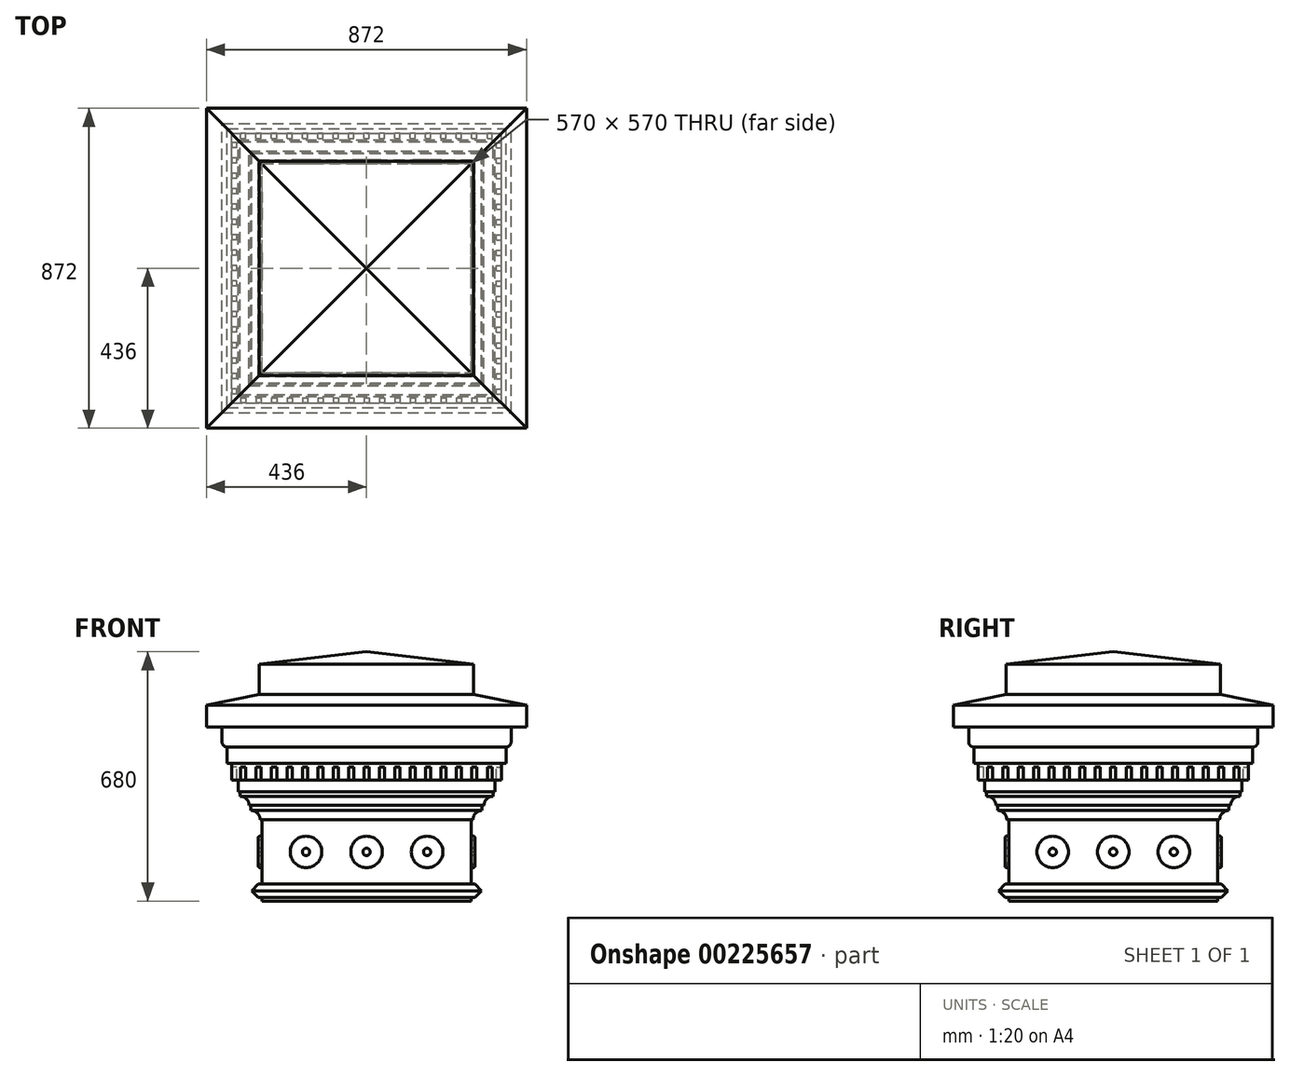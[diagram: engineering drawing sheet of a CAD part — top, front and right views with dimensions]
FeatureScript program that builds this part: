
annotation { "Feature Type Name" : "Feature", "Feature Type Description" : "" }
export const myFeature = defineFeature(function(context is Context, id is Id, definition is map)
    precondition{}
    {
        {
            var Q0;
            Q0=qCreatedBy(makeId("Front.planeOp"),FACE);
            var sketch = newSketch(context, id + "F0", { "sketchPlane" : qUnion([Q0])});
            skLineSegment(sketch, "E0", {"start": v(0, 0) * mm, "end": v(0, 350) * mm});
            skLineSegment(sketch, "E1", {"start": v(0, 350) * mm, "end": v(292, 315.9) * mm});
            skLineSegment(sketch, "E2", {"start": v(292, 315.9) * mm, "end": v(292, 233.9) * mm});
            skLineSegment(sketch, "E3", {"start": v(292, 233.9) * mm, "end": v(436, 204) * mm});
            skLineSegment(sketch, "E4", {"start": v(436, 204) * mm, "end": v(436, 144) * mm});
            skLineSegment(sketch, "E5", {"start": v(436, 144) * mm, "end": v(394, 144) * mm});
            skLineSegment(sketch, "E6", {"start": v(394, 144) * mm, "end": v(394, 104) * mm});
            skArc(sketch, "E7", {"start": v(394, 104) * mm, "mid": v(389.9, 94.1) * mm, "end": v(380, 90) * mm});
            skLineSegment(sketch, "E8", {"start": v(380, 90) * mm, "end": v(380, 46) * mm});
            skLineSegment(sketch, "E9", {"start": v(380, 46) * mm, "end": v(368, 46) * mm});
            skLineSegment(sketch, "E10", {"start": v(368, 46) * mm, "end": v(368, 0) * mm});
            skLineSegment(sketch, "E11", {"start": v(368, 0) * mm, "end": v(0, 0) * mm});
            skLineSegment(sketch, "E12.MirrorCS", {"start": v(-368, 0) * mm, "end": v(0, 0) * mm});
            skLineSegment(sketch, "E13.MirrorCS", {"start": v(0, 350) * mm, "end": v(-292, 315.9) * mm});
            skLineSegment(sketch, "E14.MirrorCS", {"start": v(-436, 144) * mm, "end": v(-394, 144) * mm});
            skLineSegment(sketch, "E15.MirrorCS", {"start": v(-368, 46) * mm, "end": v(-368, 0) * mm});
            skLineSegment(sketch, "E16.MirrorCS", {"start": v(-292, 315.9) * mm, "end": v(-292, 233.9) * mm});
            skLineSegment(sketch, "E17.MirrorCS", {"start": v(-436, 204) * mm, "end": v(-436, 144) * mm});
            skLineSegment(sketch, "E18.MirrorCS", {"start": v(-380, 46) * mm, "end": v(-368, 46) * mm});
            skLineSegment(sketch, "E19.MirrorCS", {"start": v(-292, 233.9) * mm, "end": v(-436, 204) * mm});
            skLineSegment(sketch, "E20.MirrorCS", {"start": v(-380, 90) * mm, "end": v(-380, 46) * mm});
            skArc(sketch, "E21.MirrorCS", {"start": v(-394, 104) * mm, "mid": v(-389.9, 94.1) * mm, "end": v(-380, 90) * mm});
            skLineSegment(sketch, "E22.MirrorCS", {"start": v(-394, 144) * mm, "end": v(-394, 104) * mm});
            skLineSegment(sketch, "E23", {"start": v(0, 350) * mm, "end": v(0, 852.33) * mm});
            skSolve(sketch);
        }
        {
            var Q0;
            Q0=makeQuery(id+"F0.imprint","IMPRINT",FACE,{"disambiguationData":[TD([[makeQuery(id+"F0.imprint","IMPRINT",EDGE,{"derivedFrom":sQuery(id+"F0.wireOp",EDGE,"E0")}),-1.0]])]});
            var Q1;
            Q1=makeQuery(id+"F0.imprint","IMPRINT",FACE,{"disambiguationData":[TD([[makeQuery(id+"F0.imprint","IMPRINT",EDGE,{"derivedFrom":sQuery(id+"F0.wireOp",EDGE,"E0")}),1.0]])]});
            extrude(context, id + "F1", {"entities" : qUnion([Q0, Q1]), "endBound" : BoundingType.SYMMETRIC, "depth" : 900 * mm});
        }
        {
            var Q0;
            Q0=makeQuery(id+"F1.opExtrude","SWEPT_BODY",BODY,{"disambiguationData":[OSD([sQuery(id+"F0.wireOp",EDGE,"E1"),sQuery(id+"F0.wireOp",EDGE,"E2"),sQuery(id+"F0.wireOp",EDGE,"E3"),sQuery(id+"F0.wireOp",EDGE,"E4"),sQuery(id+"F0.wireOp",EDGE,"E5"),sQuery(id+"F0.wireOp",EDGE,"E6"),sQuery(id+"F0.wireOp",EDGE,"E7"),sQuery(id+"F0.wireOp",EDGE,"E8"),sQuery(id+"F0.wireOp",EDGE,"E9"),sQuery(id+"F0.wireOp",EDGE,"E10"),sQuery(id+"F0.wireOp",EDGE,"E11"),sQuery(id+"F0.wireOp",EDGE,"E12.MirrorCS"),sQuery(id+"F0.wireOp",EDGE,"E13.MirrorCS"),sQuery(id+"F0.wireOp",EDGE,"E14.MirrorCS"),sQuery(id+"F0.wireOp",EDGE,"E15.MirrorCS"),sQuery(id+"F0.wireOp",EDGE,"E16.MirrorCS"),sQuery(id+"F0.wireOp",EDGE,"E17.MirrorCS"),sQuery(id+"F0.wireOp",EDGE,"E18.MirrorCS"),sQuery(id+"F0.wireOp",EDGE,"E19.MirrorCS"),sQuery(id+"F0.wireOp",EDGE,"E20.MirrorCS"),sQuery(id+"F0.wireOp",EDGE,"E21.MirrorCS"),sQuery(id+"F0.wireOp",EDGE,"E22.MirrorCS")])]});
            var Q1;
            Q1=sQuery(id+"F0.wireOp",EDGE,"E23");
            var Q2;
            Q2=sQuery(id+"F0.wireOp",EDGE,"E23");
            transform(context, id + "F2", {"entities" : qUnion([Q0]), "transformType" : TransformType.ROTATION, "transformAxis" : qUnion([Q2]), "angle" : 90 * degree, "oppositeDirection" : true, "makeCopy" : true});
        }
        {
            var Q0;
            Q0=makeQuery(id+"F1.opExtrude","SWEPT_BODY",BODY,{"disambiguationData":[OSD([sQuery(id+"F0.wireOp",EDGE,"E1"),sQuery(id+"F0.wireOp",EDGE,"E2"),sQuery(id+"F0.wireOp",EDGE,"E3"),sQuery(id+"F0.wireOp",EDGE,"E4"),sQuery(id+"F0.wireOp",EDGE,"E5"),sQuery(id+"F0.wireOp",EDGE,"E6"),sQuery(id+"F0.wireOp",EDGE,"E7"),sQuery(id+"F0.wireOp",EDGE,"E8"),sQuery(id+"F0.wireOp",EDGE,"E9"),sQuery(id+"F0.wireOp",EDGE,"E10"),sQuery(id+"F0.wireOp",EDGE,"E11"),sQuery(id+"F0.wireOp",EDGE,"E12.MirrorCS"),sQuery(id+"F0.wireOp",EDGE,"E13.MirrorCS"),sQuery(id+"F0.wireOp",EDGE,"E14.MirrorCS"),sQuery(id+"F0.wireOp",EDGE,"E15.MirrorCS"),sQuery(id+"F0.wireOp",EDGE,"E16.MirrorCS"),sQuery(id+"F0.wireOp",EDGE,"E17.MirrorCS"),sQuery(id+"F0.wireOp",EDGE,"E18.MirrorCS"),sQuery(id+"F0.wireOp",EDGE,"E19.MirrorCS"),sQuery(id+"F0.wireOp",EDGE,"E20.MirrorCS"),sQuery(id+"F0.wireOp",EDGE,"E21.MirrorCS"),sQuery(id+"F0.wireOp",EDGE,"E22.MirrorCS")])]});
            var Q1;
            Q1=makeQuery(id+"F2.opPattern","COPY",BODY,{"derivedFrom":makeQuery(id+"F1.opExtrude","SWEPT_BODY",BODY,{"disambiguationData":[OSD([sQuery(id+"F0.wireOp",EDGE,"E1"),sQuery(id+"F0.wireOp",EDGE,"E2"),sQuery(id+"F0.wireOp",EDGE,"E3"),sQuery(id+"F0.wireOp",EDGE,"E4"),sQuery(id+"F0.wireOp",EDGE,"E5"),sQuery(id+"F0.wireOp",EDGE,"E6"),sQuery(id+"F0.wireOp",EDGE,"E7"),sQuery(id+"F0.wireOp",EDGE,"E8"),sQuery(id+"F0.wireOp",EDGE,"E9"),sQuery(id+"F0.wireOp",EDGE,"E10"),sQuery(id+"F0.wireOp",EDGE,"E11"),sQuery(id+"F0.wireOp",EDGE,"E12.MirrorCS"),sQuery(id+"F0.wireOp",EDGE,"E13.MirrorCS"),sQuery(id+"F0.wireOp",EDGE,"E14.MirrorCS"),sQuery(id+"F0.wireOp",EDGE,"E15.MirrorCS"),sQuery(id+"F0.wireOp",EDGE,"E16.MirrorCS"),sQuery(id+"F0.wireOp",EDGE,"E17.MirrorCS"),sQuery(id+"F0.wireOp",EDGE,"E18.MirrorCS"),sQuery(id+"F0.wireOp",EDGE,"E19.MirrorCS"),sQuery(id+"F0.wireOp",EDGE,"E20.MirrorCS"),sQuery(id+"F0.wireOp",EDGE,"E21.MirrorCS"),sQuery(id+"F0.wireOp",EDGE,"E22.MirrorCS")])]}),"instanceName":"1"});
            booleanBodies(context, id + "F3", {"operationType" : BooleanOperationType.INTERSECTION, "tools" : qUnion([Q0, Q1])});
        }
        {
            var Q0;
            Q0=qCreatedBy(makeId("Front.planeOp"),FACE);
            var sketch = newSketch(context, id + "F4", { "sketchPlane" : qUnion([Q0])});
            skLineSegment(sketch, "E24", {"start": v(0, 0) * mm, "end": v(-350, 0) * mm});
            skLineSegment(sketch, "E25", {"start": v(-350, 0) * mm, "end": v(-350, -32) * mm});
            skLineSegment(sketch, "E26", {"start": v(-345, -32) * mm, "end": v(-350, -32) * mm});
            skLineSegment(sketch, "E27", {"start": v(-345, -32) * mm, "end": v(-345, -44) * mm});
            skLineSegment(sketch, "E28", {"start": v(-345, -44) * mm, "end": v(-345, -69) * mm});
            skArc(sketch, "E29", {"start": v(-345, -44) * mm, "mid": v(-327.32, -51.32) * mm, "end": v(-320, -69) * mm});
            skLineSegment(sketch, "E30", {"start": v(-320, -69) * mm, "end": v(-315, -69) * mm});
            skLineSegment(sketch, "E31", {"start": v(-315, -69) * mm, "end": v(-315, -83) * mm});
            skLineSegment(sketch, "E32", {"start": v(-315, -83) * mm, "end": v(-315, -108) * mm});
            skArc(sketch, "E33", {"start": v(-315, -83) * mm, "mid": v(-297.32, -90.32) * mm, "end": v(-290, -108) * mm});
            skLineSegment(sketch, "E34", {"start": v(-290, -108) * mm, "end": v(-285, -108) * mm});
            skLineSegment(sketch, "E35", {"start": v(-285, -108) * mm, "end": v(-285, -284) * mm});
            skLineSegment(sketch, "E36", {"start": v(-285, -284) * mm, "end": v(-295, -284) * mm});
            skLineSegment(sketch, "E37", {"start": v(-295, -284) * mm, "end": v(-313, -302) * mm});
            skLineSegment(sketch, "E38", {"start": v(-313, -302) * mm, "end": v(-295, -320) * mm});
            skLineSegment(sketch, "E39", {"start": v(-295, -320) * mm, "end": v(-285, -320) * mm});
            skLineSegment(sketch, "E40", {"start": v(-285, -320) * mm, "end": v(-285, -330) * mm});
            skLineSegment(sketch, "E41", {"start": v(-285, -330) * mm, "end": v(0, -330) * mm});
            skLineSegment(sketch, "E42", {"start": v(0, 0) * mm, "end": v(0, -330) * mm});
            skLineSegment(sketch, "E43.MirrorCS", {"start": v(0, 0) * mm, "end": v(350, 0) * mm});
            skLineSegment(sketch, "E44.MirrorCS", {"start": v(350, 0) * mm, "end": v(350, -32) * mm});
            skLineSegment(sketch, "E45.MirrorCS", {"start": v(345, -32) * mm, "end": v(350, -32) * mm});
            skLineSegment(sketch, "E46.MirrorCS", {"start": v(345, -32) * mm, "end": v(345, -44) * mm});
            skArc(sketch, "E47.MirrorCS", {"start": v(345, -44) * mm, "mid": v(327.32, -51.32) * mm, "end": v(320, -69) * mm});
            skLineSegment(sketch, "E48.MirrorCS", {"start": v(320, -69) * mm, "end": v(315, -69) * mm});
            skLineSegment(sketch, "E49.MirrorCS", {"start": v(315, -69) * mm, "end": v(315, -83) * mm});
            skArc(sketch, "E50.MirrorCS", {"start": v(315, -83) * mm, "mid": v(297.32, -90.32) * mm, "end": v(290, -108) * mm});
            skLineSegment(sketch, "E51.MirrorCS", {"start": v(290, -108) * mm, "end": v(285, -108) * mm});
            skLineSegment(sketch, "E52.MirrorCS", {"start": v(285, -108) * mm, "end": v(285, -284) * mm});
            skLineSegment(sketch, "E53.MirrorCS", {"start": v(285, -284) * mm, "end": v(295, -284) * mm});
            skLineSegment(sketch, "E54.MirrorCS", {"start": v(295, -284) * mm, "end": v(313, -302) * mm});
            skLineSegment(sketch, "E55.MirrorCS", {"start": v(313, -302) * mm, "end": v(295, -320) * mm});
            skLineSegment(sketch, "E56.MirrorCS", {"start": v(295, -320) * mm, "end": v(285, -320) * mm});
            skLineSegment(sketch, "E57.MirrorCS", {"start": v(285, -320) * mm, "end": v(285, -330) * mm});
            skLineSegment(sketch, "E58.MirrorCS", {"start": v(285, -330) * mm, "end": v(0, -330) * mm});
            skSolve(sketch);
        }
        {
            var Q0;
            Q0=makeQuery(id+"F4.imprint","IMPRINT",FACE,{"disambiguationData":[TD([[makeQuery(id+"F4.imprint","IMPRINT",EDGE,{"derivedFrom":sQuery(id+"F4.wireOp",EDGE,"E42")}),1.0]])]});
            var Q1;
            Q1=makeQuery(id+"F4.imprint","IMPRINT",FACE,{"disambiguationData":[TD([[makeQuery(id+"F4.imprint","IMPRINT",EDGE,{"derivedFrom":sQuery(id+"F4.wireOp",EDGE,"E24")}),1.0]])]});
            extrude(context, id + "F5", {"entities" : qUnion([Q0, Q1]), "endBound" : BoundingType.SYMMETRIC, "depth" : 900 * mm});
        }
        {
            var Q0;
            Q0=makeQuery(id+"F5.opExtrude","SWEPT_BODY",BODY,{"disambiguationData":[OSD([sQuery(id+"F4.wireOp",EDGE,"E24"),sQuery(id+"F4.wireOp",EDGE,"E25"),sQuery(id+"F4.wireOp",EDGE,"E26"),sQuery(id+"F4.wireOp",EDGE,"E27"),sQuery(id+"F4.wireOp",EDGE,"E29"),sQuery(id+"F4.wireOp",EDGE,"E30"),sQuery(id+"F4.wireOp",EDGE,"E31"),sQuery(id+"F4.wireOp",EDGE,"E33"),sQuery(id+"F4.wireOp",EDGE,"E34"),sQuery(id+"F4.wireOp",EDGE,"E35"),sQuery(id+"F4.wireOp",EDGE,"E36"),sQuery(id+"F4.wireOp",EDGE,"E37"),sQuery(id+"F4.wireOp",EDGE,"E38"),sQuery(id+"F4.wireOp",EDGE,"E39"),sQuery(id+"F4.wireOp",EDGE,"E40"),sQuery(id+"F4.wireOp",EDGE,"E41"),sQuery(id+"F4.wireOp",EDGE,"E43.MirrorCS"),sQuery(id+"F4.wireOp",EDGE,"E44.MirrorCS"),sQuery(id+"F4.wireOp",EDGE,"E45.MirrorCS"),sQuery(id+"F4.wireOp",EDGE,"E46.MirrorCS"),sQuery(id+"F4.wireOp",EDGE,"E47.MirrorCS"),sQuery(id+"F4.wireOp",EDGE,"E48.MirrorCS"),sQuery(id+"F4.wireOp",EDGE,"E49.MirrorCS"),sQuery(id+"F4.wireOp",EDGE,"E50.MirrorCS"),sQuery(id+"F4.wireOp",EDGE,"E51.MirrorCS"),sQuery(id+"F4.wireOp",EDGE,"E52.MirrorCS"),sQuery(id+"F4.wireOp",EDGE,"E53.MirrorCS"),sQuery(id+"F4.wireOp",EDGE,"E54.MirrorCS"),sQuery(id+"F4.wireOp",EDGE,"E55.MirrorCS"),sQuery(id+"F4.wireOp",EDGE,"E56.MirrorCS"),sQuery(id+"F4.wireOp",EDGE,"E57.MirrorCS"),sQuery(id+"F4.wireOp",EDGE,"E58.MirrorCS")])]});
            var Q1;
            Q1=sQuery(id+"F4.wireOp",EDGE,"E42");
            transform(context, id + "F6", {"entities" : qUnion([Q0]), "transformType" : TransformType.ROTATION, "transformAxis" : qUnion([Q1]), "angle" : 90 * degree, "makeCopy" : true});
        }
        {
            var Q0;
            Q0=makeQuery(id+"F5.opExtrude","SWEPT_BODY",BODY,{"disambiguationData":[OSD([sQuery(id+"F4.wireOp",EDGE,"E24"),sQuery(id+"F4.wireOp",EDGE,"E25"),sQuery(id+"F4.wireOp",EDGE,"E26"),sQuery(id+"F4.wireOp",EDGE,"E27"),sQuery(id+"F4.wireOp",EDGE,"E29"),sQuery(id+"F4.wireOp",EDGE,"E30"),sQuery(id+"F4.wireOp",EDGE,"E31"),sQuery(id+"F4.wireOp",EDGE,"E33"),sQuery(id+"F4.wireOp",EDGE,"E34"),sQuery(id+"F4.wireOp",EDGE,"E35"),sQuery(id+"F4.wireOp",EDGE,"E36"),sQuery(id+"F4.wireOp",EDGE,"E37"),sQuery(id+"F4.wireOp",EDGE,"E38"),sQuery(id+"F4.wireOp",EDGE,"E39"),sQuery(id+"F4.wireOp",EDGE,"E40"),sQuery(id+"F4.wireOp",EDGE,"E41"),sQuery(id+"F4.wireOp",EDGE,"E43.MirrorCS"),sQuery(id+"F4.wireOp",EDGE,"E44.MirrorCS"),sQuery(id+"F4.wireOp",EDGE,"E45.MirrorCS"),sQuery(id+"F4.wireOp",EDGE,"E46.MirrorCS"),sQuery(id+"F4.wireOp",EDGE,"E47.MirrorCS"),sQuery(id+"F4.wireOp",EDGE,"E48.MirrorCS"),sQuery(id+"F4.wireOp",EDGE,"E49.MirrorCS"),sQuery(id+"F4.wireOp",EDGE,"E50.MirrorCS"),sQuery(id+"F4.wireOp",EDGE,"E51.MirrorCS"),sQuery(id+"F4.wireOp",EDGE,"E52.MirrorCS"),sQuery(id+"F4.wireOp",EDGE,"E53.MirrorCS"),sQuery(id+"F4.wireOp",EDGE,"E54.MirrorCS"),sQuery(id+"F4.wireOp",EDGE,"E55.MirrorCS"),sQuery(id+"F4.wireOp",EDGE,"E56.MirrorCS"),sQuery(id+"F4.wireOp",EDGE,"E57.MirrorCS"),sQuery(id+"F4.wireOp",EDGE,"E58.MirrorCS")])]});
            var Q1;
            Q1=makeQuery(id+"F6.opPattern","COPY",BODY,{"derivedFrom":makeQuery(id+"F5.opExtrude","SWEPT_BODY",BODY,{"disambiguationData":[OSD([sQuery(id+"F4.wireOp",EDGE,"E24"),sQuery(id+"F4.wireOp",EDGE,"E25"),sQuery(id+"F4.wireOp",EDGE,"E26"),sQuery(id+"F4.wireOp",EDGE,"E27"),sQuery(id+"F4.wireOp",EDGE,"E29"),sQuery(id+"F4.wireOp",EDGE,"E30"),sQuery(id+"F4.wireOp",EDGE,"E31"),sQuery(id+"F4.wireOp",EDGE,"E33"),sQuery(id+"F4.wireOp",EDGE,"E34"),sQuery(id+"F4.wireOp",EDGE,"E35"),sQuery(id+"F4.wireOp",EDGE,"E36"),sQuery(id+"F4.wireOp",EDGE,"E37"),sQuery(id+"F4.wireOp",EDGE,"E38"),sQuery(id+"F4.wireOp",EDGE,"E39"),sQuery(id+"F4.wireOp",EDGE,"E40"),sQuery(id+"F4.wireOp",EDGE,"E41"),sQuery(id+"F4.wireOp",EDGE,"E43.MirrorCS"),sQuery(id+"F4.wireOp",EDGE,"E44.MirrorCS"),sQuery(id+"F4.wireOp",EDGE,"E45.MirrorCS"),sQuery(id+"F4.wireOp",EDGE,"E46.MirrorCS"),sQuery(id+"F4.wireOp",EDGE,"E47.MirrorCS"),sQuery(id+"F4.wireOp",EDGE,"E48.MirrorCS"),sQuery(id+"F4.wireOp",EDGE,"E49.MirrorCS"),sQuery(id+"F4.wireOp",EDGE,"E50.MirrorCS"),sQuery(id+"F4.wireOp",EDGE,"E51.MirrorCS"),sQuery(id+"F4.wireOp",EDGE,"E52.MirrorCS"),sQuery(id+"F4.wireOp",EDGE,"E53.MirrorCS"),sQuery(id+"F4.wireOp",EDGE,"E54.MirrorCS"),sQuery(id+"F4.wireOp",EDGE,"E55.MirrorCS"),sQuery(id+"F4.wireOp",EDGE,"E56.MirrorCS"),sQuery(id+"F4.wireOp",EDGE,"E57.MirrorCS"),sQuery(id+"F4.wireOp",EDGE,"E58.MirrorCS")])]}),"instanceName":"1"});
            booleanBodies(context, id + "F7", {"operationType" : BooleanOperationType.INTERSECTION, "tools" : qUnion([Q0, Q1])});
        }
        {
            var Q0;
            Q0=makeQuery(id+"F2.opPattern","COPY",FACE,{"derivedFrom":makeQuery(id+"F1.opExtrude","SWEPT_FACE",FACE,{"disambiguationData":[OSD([sQuery(id+"F0.wireOp",EDGE,"E10")])]}),"instanceName":"1"});
            var sketch = newSketch(context, id + "F8", { "sketchPlane" : qUnion([Q0])});
            skLineSegment(sketch, "E59", {"start": v(0, 0) * mm, "end": v(0, 36) * mm});
            skLineSegment(sketch, "E60", {"start": v(0, 36) * mm, "end": v(-7, 36) * mm});
            skLineSegment(sketch, "E61", {"start": v(-7, 36) * mm, "end": v(-7, 0) * mm});
            skLineSegment(sketch, "E62", {"start": v(-7, 0) * mm, "end": v(0, 0) * mm});
            skLineSegment(sketch, "E63.MirrorCS", {"start": v(0, 36) * mm, "end": v(7, 36) * mm});
            skLineSegment(sketch, "E64.MirrorCS", {"start": v(7, 36) * mm, "end": v(7, 0) * mm});
            skLineSegment(sketch, "E65.MirrorCS", {"start": v(7, 0) * mm, "end": v(0, 0) * mm});
            skLineSegment(sketch, "E66.1.0.0", {"start": v(35, 36) * mm, "end": v(35, 0) * mm});
            skLineSegment(sketch, "E66.1.0.1", {"start": v(35, 0) * mm, "end": v(42, 0) * mm});
            skLineSegment(sketch, "E66.1.0.2", {"start": v(42, 36) * mm, "end": v(35, 36) * mm});
            skLineSegment(sketch, "E66.1.0.3", {"start": v(49, 36) * mm, "end": v(49, 0) * mm});
            skLineSegment(sketch, "E66.1.0.4", {"start": v(49, 0) * mm, "end": v(42, 0) * mm});
            skLineSegment(sketch, "E66.1.0.5", {"start": v(42, 36) * mm, "end": v(49, 36) * mm});
            skLineSegment(sketch, "E66.2.0.0", {"start": v(77, 36) * mm, "end": v(77, 0) * mm});
            skLineSegment(sketch, "E66.2.0.1", {"start": v(77, 0) * mm, "end": v(84, 0) * mm});
            skLineSegment(sketch, "E66.2.0.2", {"start": v(84, 36) * mm, "end": v(77, 36) * mm});
            skLineSegment(sketch, "E66.2.0.3", {"start": v(91, 36) * mm, "end": v(91, 0) * mm});
            skLineSegment(sketch, "E66.2.0.4", {"start": v(91, 0) * mm, "end": v(84, 0) * mm});
            skLineSegment(sketch, "E66.2.0.5", {"start": v(84, 36) * mm, "end": v(91, 36) * mm});
            skLineSegment(sketch, "E66.3.0.0", {"start": v(119, 36) * mm, "end": v(119, 0) * mm});
            skLineSegment(sketch, "E66.3.0.1", {"start": v(119, 0) * mm, "end": v(126, 0) * mm});
            skLineSegment(sketch, "E66.3.0.2", {"start": v(126, 36) * mm, "end": v(119, 36) * mm});
            skLineSegment(sketch, "E66.3.0.3", {"start": v(133, 36) * mm, "end": v(133, 0) * mm});
            skLineSegment(sketch, "E66.3.0.4", {"start": v(133, 0) * mm, "end": v(126, 0) * mm});
            skLineSegment(sketch, "E66.3.0.5", {"start": v(126, 36) * mm, "end": v(133, 36) * mm});
            skLineSegment(sketch, "E66.4.0.0", {"start": v(161, 36) * mm, "end": v(161, 0) * mm});
            skLineSegment(sketch, "E66.4.0.1", {"start": v(161, 0) * mm, "end": v(168, 0) * mm});
            skLineSegment(sketch, "E66.4.0.2", {"start": v(168, 36) * mm, "end": v(161, 36) * mm});
            skLineSegment(sketch, "E66.4.0.3", {"start": v(175, 36) * mm, "end": v(175, 0) * mm});
            skLineSegment(sketch, "E66.4.0.4", {"start": v(175, 0) * mm, "end": v(168, 0) * mm});
            skLineSegment(sketch, "E66.4.0.5", {"start": v(168, 36) * mm, "end": v(175, 36) * mm});
            skLineSegment(sketch, "E66.5.0.0", {"start": v(203, 36) * mm, "end": v(203, 0) * mm});
            skLineSegment(sketch, "E66.5.0.1", {"start": v(203, 0) * mm, "end": v(210, 0) * mm});
            skLineSegment(sketch, "E66.5.0.2", {"start": v(210, 36) * mm, "end": v(203, 36) * mm});
            skLineSegment(sketch, "E66.5.0.3", {"start": v(217, 36) * mm, "end": v(217, 0) * mm});
            skLineSegment(sketch, "E66.5.0.4", {"start": v(217, 0) * mm, "end": v(210, 0) * mm});
            skLineSegment(sketch, "E66.5.0.5", {"start": v(210, 36) * mm, "end": v(217, 36) * mm});
            skLineSegment(sketch, "E66.6.0.0", {"start": v(245, 36) * mm, "end": v(245, 0) * mm});
            skLineSegment(sketch, "E66.6.0.1", {"start": v(245, 0) * mm, "end": v(252, 0) * mm});
            skLineSegment(sketch, "E66.6.0.2", {"start": v(252, 36) * mm, "end": v(245, 36) * mm});
            skLineSegment(sketch, "E66.6.0.3", {"start": v(259, 36) * mm, "end": v(259, 0) * mm});
            skLineSegment(sketch, "E66.6.0.4", {"start": v(259, 0) * mm, "end": v(252, 0) * mm});
            skLineSegment(sketch, "E66.6.0.5", {"start": v(252, 36) * mm, "end": v(259, 36) * mm});
            skLineSegment(sketch, "E66.7.0.0", {"start": v(287, 36) * mm, "end": v(287, 0) * mm});
            skLineSegment(sketch, "E66.7.0.1", {"start": v(287, 0) * mm, "end": v(294, 0) * mm});
            skLineSegment(sketch, "E66.7.0.2", {"start": v(294, 36) * mm, "end": v(287, 36) * mm});
            skLineSegment(sketch, "E66.7.0.3", {"start": v(301, 36) * mm, "end": v(301, 0) * mm});
            skLineSegment(sketch, "E66.7.0.4", {"start": v(301, 0) * mm, "end": v(294, 0) * mm});
            skLineSegment(sketch, "E66.7.0.5", {"start": v(294, 36) * mm, "end": v(301, 36) * mm});
            skLineSegment(sketch, "E66.8.0.0", {"start": v(329, 36) * mm, "end": v(329, 0) * mm});
            skLineSegment(sketch, "E66.8.0.1", {"start": v(329, 0) * mm, "end": v(336, 0) * mm});
            skLineSegment(sketch, "E66.8.0.2", {"start": v(336, 36) * mm, "end": v(329, 36) * mm});
            skLineSegment(sketch, "E66.8.0.3", {"start": v(343, 36) * mm, "end": v(343, 0) * mm});
            skLineSegment(sketch, "E66.8.0.4", {"start": v(343, 0) * mm, "end": v(336, 0) * mm});
            skLineSegment(sketch, "E66.8.0.5", {"start": v(336, 36) * mm, "end": v(343, 36) * mm});
            skLineSegment(sketch, "E66.direction1", {"start": v(-7, 36) * mm, "end": v(35, 36) * mm, "construction": true});
            skLineSegment(sketch, "E67.1.0.0", {"start": v(-49, 36) * mm, "end": v(-49, 0) * mm});
            skLineSegment(sketch, "E67.1.0.1", {"start": v(-49, 0) * mm, "end": v(-42, 0) * mm});
            skLineSegment(sketch, "E67.1.0.2", {"start": v(-42, 36) * mm, "end": v(-49, 36) * mm});
            skLineSegment(sketch, "E67.1.0.3", {"start": v(-35, 36) * mm, "end": v(-35, 0) * mm});
            skLineSegment(sketch, "E67.1.0.4", {"start": v(-35, 0) * mm, "end": v(-42, 0) * mm});
            skLineSegment(sketch, "E67.1.0.5", {"start": v(-42, 36) * mm, "end": v(-35, 36) * mm});
            skLineSegment(sketch, "E67.2.0.0", {"start": v(-91, 36) * mm, "end": v(-91, 0) * mm});
            skLineSegment(sketch, "E67.2.0.1", {"start": v(-91, 0) * mm, "end": v(-84, 0) * mm});
            skLineSegment(sketch, "E67.2.0.2", {"start": v(-84, 36) * mm, "end": v(-91, 36) * mm});
            skLineSegment(sketch, "E67.2.0.3", {"start": v(-77, 36) * mm, "end": v(-77, 0) * mm});
            skLineSegment(sketch, "E67.2.0.4", {"start": v(-77, 0) * mm, "end": v(-84, 0) * mm});
            skLineSegment(sketch, "E67.2.0.5", {"start": v(-84, 36) * mm, "end": v(-77, 36) * mm});
            skLineSegment(sketch, "E67.3.0.0", {"start": v(-133, 36) * mm, "end": v(-133, 0) * mm});
            skLineSegment(sketch, "E67.3.0.1", {"start": v(-133, 0) * mm, "end": v(-126, 0) * mm});
            skLineSegment(sketch, "E67.3.0.2", {"start": v(-126, 36) * mm, "end": v(-133, 36) * mm});
            skLineSegment(sketch, "E67.3.0.3", {"start": v(-119, 36) * mm, "end": v(-119, 0) * mm});
            skLineSegment(sketch, "E67.3.0.4", {"start": v(-119, 0) * mm, "end": v(-126, 0) * mm});
            skLineSegment(sketch, "E67.3.0.5", {"start": v(-126, 36) * mm, "end": v(-119, 36) * mm});
            skLineSegment(sketch, "E67.4.0.0", {"start": v(-175, 36) * mm, "end": v(-175, 0) * mm});
            skLineSegment(sketch, "E67.4.0.1", {"start": v(-175, 0) * mm, "end": v(-168, 0) * mm});
            skLineSegment(sketch, "E67.4.0.2", {"start": v(-168, 36) * mm, "end": v(-175, 36) * mm});
            skLineSegment(sketch, "E67.4.0.3", {"start": v(-161, 36) * mm, "end": v(-161, 0) * mm});
            skLineSegment(sketch, "E67.4.0.4", {"start": v(-161, 0) * mm, "end": v(-168, 0) * mm});
            skLineSegment(sketch, "E67.4.0.5", {"start": v(-168, 36) * mm, "end": v(-161, 36) * mm});
            skLineSegment(sketch, "E67.5.0.0", {"start": v(-217, 36) * mm, "end": v(-217, 0) * mm});
            skLineSegment(sketch, "E67.5.0.1", {"start": v(-217, 0) * mm, "end": v(-210, 0) * mm});
            skLineSegment(sketch, "E67.5.0.2", {"start": v(-210, 36) * mm, "end": v(-217, 36) * mm});
            skLineSegment(sketch, "E67.5.0.3", {"start": v(-203, 36) * mm, "end": v(-203, 0) * mm});
            skLineSegment(sketch, "E67.5.0.4", {"start": v(-203, 0) * mm, "end": v(-210, 0) * mm});
            skLineSegment(sketch, "E67.5.0.5", {"start": v(-210, 36) * mm, "end": v(-203, 36) * mm});
            skLineSegment(sketch, "E67.6.0.0", {"start": v(-259, 36) * mm, "end": v(-259, 0) * mm});
            skLineSegment(sketch, "E67.6.0.1", {"start": v(-259, 0) * mm, "end": v(-252, 0) * mm});
            skLineSegment(sketch, "E67.6.0.2", {"start": v(-252, 36) * mm, "end": v(-259, 36) * mm});
            skLineSegment(sketch, "E67.6.0.3", {"start": v(-245, 36) * mm, "end": v(-245, 0) * mm});
            skLineSegment(sketch, "E67.6.0.4", {"start": v(-245, 0) * mm, "end": v(-252, 0) * mm});
            skLineSegment(sketch, "E67.6.0.5", {"start": v(-252, 36) * mm, "end": v(-245, 36) * mm});
            skLineSegment(sketch, "E67.7.0.0", {"start": v(-301, 36) * mm, "end": v(-301, 0) * mm});
            skLineSegment(sketch, "E67.7.0.1", {"start": v(-301, 0) * mm, "end": v(-294, 0) * mm});
            skLineSegment(sketch, "E67.7.0.2", {"start": v(-294, 36) * mm, "end": v(-301, 36) * mm});
            skLineSegment(sketch, "E67.7.0.3", {"start": v(-287, 36) * mm, "end": v(-287, 0) * mm});
            skLineSegment(sketch, "E67.7.0.4", {"start": v(-287, 0) * mm, "end": v(-294, 0) * mm});
            skLineSegment(sketch, "E67.7.0.5", {"start": v(-294, 36) * mm, "end": v(-287, 36) * mm});
            skLineSegment(sketch, "E67.8.0.0", {"start": v(-343, 36) * mm, "end": v(-343, 0) * mm});
            skLineSegment(sketch, "E67.8.0.1", {"start": v(-343, 0) * mm, "end": v(-336, 0) * mm});
            skLineSegment(sketch, "E67.8.0.2", {"start": v(-336, 36) * mm, "end": v(-343, 36) * mm});
            skLineSegment(sketch, "E67.8.0.3", {"start": v(-329, 36) * mm, "end": v(-329, 0) * mm});
            skLineSegment(sketch, "E67.8.0.4", {"start": v(-329, 0) * mm, "end": v(-336, 0) * mm});
            skLineSegment(sketch, "E67.8.0.5", {"start": v(-336, 36) * mm, "end": v(-329, 36) * mm});
            skLineSegment(sketch, "E67.direction1", {"start": v(-7, 36) * mm, "end": v(-49, 36) * mm, "construction": true});
            skSolve(sketch);
        }
        {
            var Q0;
            Q0=makeQuery(id+"F1.opExtrude","SWEPT_FACE",FACE,{"disambiguationData":[OSD([sQuery(id+"F0.wireOp",EDGE,"E10")])]});
            var sketch = newSketch(context, id + "F9", { "sketchPlane" : qUnion([Q0])});
            skLineSegment(sketch, "E68", {"start": v(0, 0) * mm, "end": v(-7, 0) * mm});
            skLineSegment(sketch, "E69", {"start": v(-7, 0) * mm, "end": v(-7, 36) * mm});
            skLineSegment(sketch, "E70", {"start": v(-7, 36) * mm, "end": v(7, 36) * mm});
            skLineSegment(sketch, "E71", {"start": v(7, 36) * mm, "end": v(7, 0) * mm});
            skLineSegment(sketch, "E72", {"start": v(7, 0) * mm, "end": v(0, 0) * mm});
            skLineSegment(sketch, "E73.1.0.0", {"start": v(35, 0) * mm, "end": v(35, 36) * mm});
            skLineSegment(sketch, "E73.1.0.1", {"start": v(49, 36) * mm, "end": v(49, 0) * mm});
            skLineSegment(sketch, "E73.1.0.2", {"start": v(49, 0) * mm, "end": v(42, 0) * mm});
            skLineSegment(sketch, "E73.1.0.3", {"start": v(35, 36) * mm, "end": v(49, 36) * mm});
            skLineSegment(sketch, "E73.1.0.4", {"start": v(42, 0) * mm, "end": v(35, 0) * mm});
            skLineSegment(sketch, "E73.2.0.0", {"start": v(77, 0) * mm, "end": v(77, 36) * mm});
            skLineSegment(sketch, "E73.2.0.1", {"start": v(91, 36) * mm, "end": v(91, 0) * mm});
            skLineSegment(sketch, "E73.2.0.2", {"start": v(91, 0) * mm, "end": v(84, 0) * mm});
            skLineSegment(sketch, "E73.2.0.3", {"start": v(77, 36) * mm, "end": v(91, 36) * mm});
            skLineSegment(sketch, "E73.2.0.4", {"start": v(84, 0) * mm, "end": v(77, 0) * mm});
            skLineSegment(sketch, "E73.3.0.0", {"start": v(119, 0) * mm, "end": v(119, 36) * mm});
            skLineSegment(sketch, "E73.3.0.1", {"start": v(133, 36) * mm, "end": v(133, 0) * mm});
            skLineSegment(sketch, "E73.3.0.2", {"start": v(133, 0) * mm, "end": v(126, 0) * mm});
            skLineSegment(sketch, "E73.3.0.3", {"start": v(119, 36) * mm, "end": v(133, 36) * mm});
            skLineSegment(sketch, "E73.3.0.4", {"start": v(126, 0) * mm, "end": v(119, 0) * mm});
            skLineSegment(sketch, "E73.4.0.0", {"start": v(161, 0) * mm, "end": v(161, 36) * mm});
            skLineSegment(sketch, "E73.4.0.1", {"start": v(175, 36) * mm, "end": v(175, 0) * mm});
            skLineSegment(sketch, "E73.4.0.2", {"start": v(175, 0) * mm, "end": v(168, 0) * mm});
            skLineSegment(sketch, "E73.4.0.3", {"start": v(161, 36) * mm, "end": v(175, 36) * mm});
            skLineSegment(sketch, "E73.4.0.4", {"start": v(168, 0) * mm, "end": v(161, 0) * mm});
            skLineSegment(sketch, "E73.5.0.0", {"start": v(203, 0) * mm, "end": v(203, 36) * mm});
            skLineSegment(sketch, "E73.5.0.1", {"start": v(217, 36) * mm, "end": v(217, 0) * mm});
            skLineSegment(sketch, "E73.5.0.2", {"start": v(217, 0) * mm, "end": v(210, 0) * mm});
            skLineSegment(sketch, "E73.5.0.3", {"start": v(203, 36) * mm, "end": v(217, 36) * mm});
            skLineSegment(sketch, "E73.5.0.4", {"start": v(210, 0) * mm, "end": v(203, 0) * mm});
            skLineSegment(sketch, "E73.6.0.0", {"start": v(245, 0) * mm, "end": v(245, 36) * mm});
            skLineSegment(sketch, "E73.6.0.1", {"start": v(259, 36) * mm, "end": v(259, 0) * mm});
            skLineSegment(sketch, "E73.6.0.2", {"start": v(259, 0) * mm, "end": v(252, 0) * mm});
            skLineSegment(sketch, "E73.6.0.3", {"start": v(245, 36) * mm, "end": v(259, 36) * mm});
            skLineSegment(sketch, "E73.6.0.4", {"start": v(252, 0) * mm, "end": v(245, 0) * mm});
            skLineSegment(sketch, "E73.7.0.0", {"start": v(287, 0) * mm, "end": v(287, 36) * mm});
            skLineSegment(sketch, "E73.7.0.1", {"start": v(301, 36) * mm, "end": v(301, 0) * mm});
            skLineSegment(sketch, "E73.7.0.2", {"start": v(301, 0) * mm, "end": v(294, 0) * mm});
            skLineSegment(sketch, "E73.7.0.3", {"start": v(287, 36) * mm, "end": v(301, 36) * mm});
            skLineSegment(sketch, "E73.7.0.4", {"start": v(294, 0) * mm, "end": v(287, 0) * mm});
            skLineSegment(sketch, "E73.8.0.0", {"start": v(329, 0) * mm, "end": v(329, 36) * mm});
            skLineSegment(sketch, "E73.8.0.1", {"start": v(343, 36) * mm, "end": v(343, 0) * mm});
            skLineSegment(sketch, "E73.8.0.2", {"start": v(343, 0) * mm, "end": v(336, 0) * mm});
            skLineSegment(sketch, "E73.8.0.3", {"start": v(329, 36) * mm, "end": v(343, 36) * mm});
            skLineSegment(sketch, "E73.8.0.4", {"start": v(336, 0) * mm, "end": v(329, 0) * mm});
            skLineSegment(sketch, "E73.direction1", {"start": v(-7, 36) * mm, "end": v(35, 36) * mm, "construction": true});
            skLineSegment(sketch, "E74.1.0.0", {"start": v(-49, 0) * mm, "end": v(-49, 36) * mm});
            skLineSegment(sketch, "E74.1.0.1", {"start": v(-35, 36) * mm, "end": v(-35, 0) * mm});
            skLineSegment(sketch, "E74.1.0.2", {"start": v(-35, 0) * mm, "end": v(-42, 0) * mm});
            skLineSegment(sketch, "E74.1.0.3", {"start": v(-49, 36) * mm, "end": v(-35, 36) * mm});
            skLineSegment(sketch, "E74.1.0.4", {"start": v(-42, 0) * mm, "end": v(-49, 0) * mm});
            skLineSegment(sketch, "E74.2.0.0", {"start": v(-91, 0) * mm, "end": v(-91, 36) * mm});
            skLineSegment(sketch, "E74.2.0.1", {"start": v(-77, 36) * mm, "end": v(-77, 0) * mm});
            skLineSegment(sketch, "E74.2.0.2", {"start": v(-77, 0) * mm, "end": v(-84, 0) * mm});
            skLineSegment(sketch, "E74.2.0.3", {"start": v(-91, 36) * mm, "end": v(-77, 36) * mm});
            skLineSegment(sketch, "E74.2.0.4", {"start": v(-84, 0) * mm, "end": v(-91, 0) * mm});
            skLineSegment(sketch, "E74.3.0.0", {"start": v(-133, 0) * mm, "end": v(-133, 36) * mm});
            skLineSegment(sketch, "E74.3.0.1", {"start": v(-119, 36) * mm, "end": v(-119, 0) * mm});
            skLineSegment(sketch, "E74.3.0.2", {"start": v(-119, 0) * mm, "end": v(-126, 0) * mm});
            skLineSegment(sketch, "E74.3.0.3", {"start": v(-133, 36) * mm, "end": v(-119, 36) * mm});
            skLineSegment(sketch, "E74.3.0.4", {"start": v(-126, 0) * mm, "end": v(-133, 0) * mm});
            skLineSegment(sketch, "E74.4.0.0", {"start": v(-175, 0) * mm, "end": v(-175, 36) * mm});
            skLineSegment(sketch, "E74.4.0.1", {"start": v(-161, 36) * mm, "end": v(-161, 0) * mm});
            skLineSegment(sketch, "E74.4.0.2", {"start": v(-161, 0) * mm, "end": v(-168, 0) * mm});
            skLineSegment(sketch, "E74.4.0.3", {"start": v(-175, 36) * mm, "end": v(-161, 36) * mm});
            skLineSegment(sketch, "E74.4.0.4", {"start": v(-168, 0) * mm, "end": v(-175, 0) * mm});
            skLineSegment(sketch, "E74.5.0.0", {"start": v(-217, 0) * mm, "end": v(-217, 36) * mm});
            skLineSegment(sketch, "E74.5.0.1", {"start": v(-203, 36) * mm, "end": v(-203, 0) * mm});
            skLineSegment(sketch, "E74.5.0.2", {"start": v(-203, 0) * mm, "end": v(-210, 0) * mm});
            skLineSegment(sketch, "E74.5.0.3", {"start": v(-217, 36) * mm, "end": v(-203, 36) * mm});
            skLineSegment(sketch, "E74.5.0.4", {"start": v(-210, 0) * mm, "end": v(-217, 0) * mm});
            skLineSegment(sketch, "E74.6.0.0", {"start": v(-259, 0) * mm, "end": v(-259, 36) * mm});
            skLineSegment(sketch, "E74.6.0.1", {"start": v(-245, 36) * mm, "end": v(-245, 0) * mm});
            skLineSegment(sketch, "E74.6.0.2", {"start": v(-245, 0) * mm, "end": v(-252, 0) * mm});
            skLineSegment(sketch, "E74.6.0.3", {"start": v(-259, 36) * mm, "end": v(-245, 36) * mm});
            skLineSegment(sketch, "E74.6.0.4", {"start": v(-252, 0) * mm, "end": v(-259, 0) * mm});
            skLineSegment(sketch, "E74.7.0.0", {"start": v(-301, 0) * mm, "end": v(-301, 36) * mm});
            skLineSegment(sketch, "E74.7.0.1", {"start": v(-287, 36) * mm, "end": v(-287, 0) * mm});
            skLineSegment(sketch, "E74.7.0.2", {"start": v(-287, 0) * mm, "end": v(-294, 0) * mm});
            skLineSegment(sketch, "E74.7.0.3", {"start": v(-301, 36) * mm, "end": v(-287, 36) * mm});
            skLineSegment(sketch, "E74.7.0.4", {"start": v(-294, 0) * mm, "end": v(-301, 0) * mm});
            skLineSegment(sketch, "E74.8.0.0", {"start": v(-343, 0) * mm, "end": v(-343, 36) * mm});
            skLineSegment(sketch, "E74.8.0.1", {"start": v(-329, 36) * mm, "end": v(-329, 0) * mm});
            skLineSegment(sketch, "E74.8.0.2", {"start": v(-329, 0) * mm, "end": v(-336, 0) * mm});
            skLineSegment(sketch, "E74.8.0.3", {"start": v(-343, 36) * mm, "end": v(-329, 36) * mm});
            skLineSegment(sketch, "E74.8.0.4", {"start": v(-336, 0) * mm, "end": v(-343, 0) * mm});
            skLineSegment(sketch, "E74.direction1", {"start": v(-7, 36) * mm, "end": v(-49, 36) * mm, "construction": true});
            skSolve(sketch);
        }
        {
            var Q0;
            Q0=makeQuery(id+"F2.opPattern","COPY",FACE,{"derivedFrom":makeQuery(id+"F1.opExtrude","SWEPT_FACE",FACE,{"disambiguationData":[OSD([sQuery(id+"F0.wireOp",EDGE,"E15.MirrorCS")])]}),"instanceName":"1"});
            var sketch = newSketch(context, id + "F10", { "sketchPlane" : qUnion([Q0])});
            skLineSegment(sketch, "E75", {"start": v(0, 0) * mm, "end": v(-7, 0) * mm});
            skLineSegment(sketch, "E76", {"start": v(-7, 0) * mm, "end": v(-7, 36) * mm});
            skLineSegment(sketch, "E77", {"start": v(-7, 36) * mm, "end": v(7, 36) * mm});
            skLineSegment(sketch, "E78", {"start": v(7, 36) * mm, "end": v(7, 0) * mm});
            skLineSegment(sketch, "E79", {"start": v(7, 0) * mm, "end": v(0, 0) * mm});
            skLineSegment(sketch, "E80.1.0.0", {"start": v(35, 0) * mm, "end": v(35, 36) * mm});
            skLineSegment(sketch, "E80.1.0.1", {"start": v(35, 36) * mm, "end": v(49, 36) * mm});
            skLineSegment(sketch, "E80.1.0.2", {"start": v(49, 0) * mm, "end": v(42, 0) * mm});
            skLineSegment(sketch, "E80.1.0.3", {"start": v(49, 36) * mm, "end": v(49, 0) * mm});
            skLineSegment(sketch, "E80.1.0.4", {"start": v(42, 0) * mm, "end": v(35, 0) * mm});
            skLineSegment(sketch, "E80.2.0.0", {"start": v(77, 0) * mm, "end": v(77, 36) * mm});
            skLineSegment(sketch, "E80.2.0.1", {"start": v(77, 36) * mm, "end": v(91, 36) * mm});
            skLineSegment(sketch, "E80.2.0.2", {"start": v(91, 0) * mm, "end": v(84, 0) * mm});
            skLineSegment(sketch, "E80.2.0.3", {"start": v(91, 36) * mm, "end": v(91, 0) * mm});
            skLineSegment(sketch, "E80.2.0.4", {"start": v(84, 0) * mm, "end": v(77, 0) * mm});
            skLineSegment(sketch, "E80.3.0.0", {"start": v(119, 0) * mm, "end": v(119, 36) * mm});
            skLineSegment(sketch, "E80.3.0.1", {"start": v(119, 36) * mm, "end": v(133, 36) * mm});
            skLineSegment(sketch, "E80.3.0.2", {"start": v(133, 0) * mm, "end": v(126, 0) * mm});
            skLineSegment(sketch, "E80.3.0.3", {"start": v(133, 36) * mm, "end": v(133, 0) * mm});
            skLineSegment(sketch, "E80.3.0.4", {"start": v(126, 0) * mm, "end": v(119, 0) * mm});
            skLineSegment(sketch, "E80.4.0.0", {"start": v(161, 0) * mm, "end": v(161, 36) * mm});
            skLineSegment(sketch, "E80.4.0.1", {"start": v(161, 36) * mm, "end": v(175, 36) * mm});
            skLineSegment(sketch, "E80.4.0.2", {"start": v(175, 0) * mm, "end": v(168, 0) * mm});
            skLineSegment(sketch, "E80.4.0.3", {"start": v(175, 36) * mm, "end": v(175, 0) * mm});
            skLineSegment(sketch, "E80.4.0.4", {"start": v(168, 0) * mm, "end": v(161, 0) * mm});
            skLineSegment(sketch, "E80.5.0.0", {"start": v(203, 0) * mm, "end": v(203, 36) * mm});
            skLineSegment(sketch, "E80.5.0.1", {"start": v(203, 36) * mm, "end": v(217, 36) * mm});
            skLineSegment(sketch, "E80.5.0.2", {"start": v(217, 0) * mm, "end": v(210, 0) * mm});
            skLineSegment(sketch, "E80.5.0.3", {"start": v(217, 36) * mm, "end": v(217, 0) * mm});
            skLineSegment(sketch, "E80.5.0.4", {"start": v(210, 0) * mm, "end": v(203, 0) * mm});
            skLineSegment(sketch, "E80.6.0.0", {"start": v(245, 0) * mm, "end": v(245, 36) * mm});
            skLineSegment(sketch, "E80.6.0.1", {"start": v(245, 36) * mm, "end": v(259, 36) * mm});
            skLineSegment(sketch, "E80.6.0.2", {"start": v(259, 0) * mm, "end": v(252, 0) * mm});
            skLineSegment(sketch, "E80.6.0.3", {"start": v(259, 36) * mm, "end": v(259, 0) * mm});
            skLineSegment(sketch, "E80.6.0.4", {"start": v(252, 0) * mm, "end": v(245, 0) * mm});
            skLineSegment(sketch, "E80.7.0.0", {"start": v(287, 0) * mm, "end": v(287, 36) * mm});
            skLineSegment(sketch, "E80.7.0.1", {"start": v(287, 36) * mm, "end": v(301, 36) * mm});
            skLineSegment(sketch, "E80.7.0.2", {"start": v(301, 0) * mm, "end": v(294, 0) * mm});
            skLineSegment(sketch, "E80.7.0.3", {"start": v(301, 36) * mm, "end": v(301, 0) * mm});
            skLineSegment(sketch, "E80.7.0.4", {"start": v(294, 0) * mm, "end": v(287, 0) * mm});
            skLineSegment(sketch, "E80.8.0.0", {"start": v(329, 0) * mm, "end": v(329, 36) * mm});
            skLineSegment(sketch, "E80.8.0.1", {"start": v(329, 36) * mm, "end": v(343, 36) * mm});
            skLineSegment(sketch, "E80.8.0.2", {"start": v(343, 0) * mm, "end": v(336, 0) * mm});
            skLineSegment(sketch, "E80.8.0.3", {"start": v(343, 36) * mm, "end": v(343, 0) * mm});
            skLineSegment(sketch, "E80.8.0.4", {"start": v(336, 0) * mm, "end": v(329, 0) * mm});
            skLineSegment(sketch, "E80.direction1", {"start": v(-7, 0) * mm, "end": v(35, 0) * mm, "construction": true});
            skLineSegment(sketch, "E81.1.0.0", {"start": v(-49, 0) * mm, "end": v(-49, 36) * mm});
            skLineSegment(sketch, "E81.1.0.1", {"start": v(-49, 36) * mm, "end": v(-35, 36) * mm});
            skLineSegment(sketch, "E81.1.0.2", {"start": v(-35, 0) * mm, "end": v(-42, 0) * mm});
            skLineSegment(sketch, "E81.1.0.3", {"start": v(-35, 36) * mm, "end": v(-35, 0) * mm});
            skLineSegment(sketch, "E81.1.0.4", {"start": v(-42, 0) * mm, "end": v(-49, 0) * mm});
            skLineSegment(sketch, "E81.2.0.0", {"start": v(-91, 0) * mm, "end": v(-91, 36) * mm});
            skLineSegment(sketch, "E81.2.0.1", {"start": v(-91, 36) * mm, "end": v(-77, 36) * mm});
            skLineSegment(sketch, "E81.2.0.2", {"start": v(-77, 0) * mm, "end": v(-84, 0) * mm});
            skLineSegment(sketch, "E81.2.0.3", {"start": v(-77, 36) * mm, "end": v(-77, 0) * mm});
            skLineSegment(sketch, "E81.2.0.4", {"start": v(-84, 0) * mm, "end": v(-91, 0) * mm});
            skLineSegment(sketch, "E81.3.0.0", {"start": v(-133, 0) * mm, "end": v(-133, 36) * mm});
            skLineSegment(sketch, "E81.3.0.1", {"start": v(-133, 36) * mm, "end": v(-119, 36) * mm});
            skLineSegment(sketch, "E81.3.0.2", {"start": v(-119, 0) * mm, "end": v(-126, 0) * mm});
            skLineSegment(sketch, "E81.3.0.3", {"start": v(-119, 36) * mm, "end": v(-119, 0) * mm});
            skLineSegment(sketch, "E81.3.0.4", {"start": v(-126, 0) * mm, "end": v(-133, 0) * mm});
            skLineSegment(sketch, "E81.4.0.0", {"start": v(-175, 0) * mm, "end": v(-175, 36) * mm});
            skLineSegment(sketch, "E81.4.0.1", {"start": v(-175, 36) * mm, "end": v(-161, 36) * mm});
            skLineSegment(sketch, "E81.4.0.2", {"start": v(-161, 0) * mm, "end": v(-168, 0) * mm});
            skLineSegment(sketch, "E81.4.0.3", {"start": v(-161, 36) * mm, "end": v(-161, 0) * mm});
            skLineSegment(sketch, "E81.4.0.4", {"start": v(-168, 0) * mm, "end": v(-175, 0) * mm});
            skLineSegment(sketch, "E81.5.0.0", {"start": v(-217, 0) * mm, "end": v(-217, 36) * mm});
            skLineSegment(sketch, "E81.5.0.1", {"start": v(-217, 36) * mm, "end": v(-203, 36) * mm});
            skLineSegment(sketch, "E81.5.0.2", {"start": v(-203, 0) * mm, "end": v(-210, 0) * mm});
            skLineSegment(sketch, "E81.5.0.3", {"start": v(-203, 36) * mm, "end": v(-203, 0) * mm});
            skLineSegment(sketch, "E81.5.0.4", {"start": v(-210, 0) * mm, "end": v(-217, 0) * mm});
            skLineSegment(sketch, "E81.6.0.0", {"start": v(-259, 0) * mm, "end": v(-259, 36) * mm});
            skLineSegment(sketch, "E81.6.0.1", {"start": v(-259, 36) * mm, "end": v(-245, 36) * mm});
            skLineSegment(sketch, "E81.6.0.2", {"start": v(-245, 0) * mm, "end": v(-252, 0) * mm});
            skLineSegment(sketch, "E81.6.0.3", {"start": v(-245, 36) * mm, "end": v(-245, 0) * mm});
            skLineSegment(sketch, "E81.6.0.4", {"start": v(-252, 0) * mm, "end": v(-259, 0) * mm});
            skLineSegment(sketch, "E81.7.0.0", {"start": v(-301, 0) * mm, "end": v(-301, 36) * mm});
            skLineSegment(sketch, "E81.7.0.1", {"start": v(-301, 36) * mm, "end": v(-287, 36) * mm});
            skLineSegment(sketch, "E81.7.0.2", {"start": v(-287, 0) * mm, "end": v(-294, 0) * mm});
            skLineSegment(sketch, "E81.7.0.3", {"start": v(-287, 36) * mm, "end": v(-287, 0) * mm});
            skLineSegment(sketch, "E81.7.0.4", {"start": v(-294, 0) * mm, "end": v(-301, 0) * mm});
            skLineSegment(sketch, "E81.8.0.0", {"start": v(-343, 0) * mm, "end": v(-343, 36) * mm});
            skLineSegment(sketch, "E81.8.0.1", {"start": v(-343, 36) * mm, "end": v(-329, 36) * mm});
            skLineSegment(sketch, "E81.8.0.2", {"start": v(-329, 0) * mm, "end": v(-336, 0) * mm});
            skLineSegment(sketch, "E81.8.0.3", {"start": v(-329, 36) * mm, "end": v(-329, 0) * mm});
            skLineSegment(sketch, "E81.8.0.4", {"start": v(-336, 0) * mm, "end": v(-343, 0) * mm});
            skLineSegment(sketch, "E81.direction1", {"start": v(0, 0) * mm, "end": v(-42, 0) * mm, "construction": true});
            skSolve(sketch);
        }
        {
            var Q0;
            Q0 = qSketchRegion(id + "F8", true);
            extrude(context, id + "F11", {"entities" : qUnion([Q0]), "operationType" : NewBodyOperationType.REMOVE, "oppositeDirection" : true, "depth" : 14 * mm});
        }
        {
            var Q0;
            Q0 = qSketchRegion(id + "F9", true);
            extrude(context, id + "F12", {"entities" : qUnion([Q0]), "operationType" : NewBodyOperationType.REMOVE, "oppositeDirection" : true, "depth" : 14 * mm});
        }
        {
            var Q0;
            Q0 = qSketchRegion(id + "F10", true);
            extrude(context, id + "F13", {"entities" : qUnion([Q0]), "operationType" : NewBodyOperationType.REMOVE, "oppositeDirection" : true, "depth" : 14 * mm});
        }
        {
            var Q0;
            Q0=makeQuery(id+"F1.opExtrude","SWEPT_FACE",FACE,{"disambiguationData":[OSD([sQuery(id+"F0.wireOp",EDGE,"E15.MirrorCS")])]});
            var sketch = newSketch(context, id + "F14", { "sketchPlane" : qUnion([Q0])});
            skLineSegment(sketch, "E82", {"start": v(0, 0) * mm, "end": v(-7, 0) * mm});
            skLineSegment(sketch, "E83", {"start": v(-7, 0) * mm, "end": v(-7, 36) * mm});
            skLineSegment(sketch, "E84", {"start": v(-7, 36) * mm, "end": v(7, 36) * mm});
            skLineSegment(sketch, "E85", {"start": v(7, 36) * mm, "end": v(7, 0) * mm});
            skLineSegment(sketch, "E86", {"start": v(7, 0) * mm, "end": v(0, 0) * mm});
            skLineSegment(sketch, "E87.1.0.0", {"start": v(49, 36) * mm, "end": v(49, 0) * mm});
            skLineSegment(sketch, "E87.1.0.1", {"start": v(35, 0) * mm, "end": v(35, 36) * mm});
            skLineSegment(sketch, "E87.1.0.2", {"start": v(42, 0) * mm, "end": v(35, 0) * mm});
            skLineSegment(sketch, "E87.1.0.3", {"start": v(35, 36) * mm, "end": v(49, 36) * mm});
            skLineSegment(sketch, "E87.1.0.4", {"start": v(49, 0) * mm, "end": v(42, 0) * mm});
            skLineSegment(sketch, "E87.2.0.0", {"start": v(91, 36) * mm, "end": v(91, 0) * mm});
            skLineSegment(sketch, "E87.2.0.1", {"start": v(77, 0) * mm, "end": v(77, 36) * mm});
            skLineSegment(sketch, "E87.2.0.2", {"start": v(84, 0) * mm, "end": v(77, 0) * mm});
            skLineSegment(sketch, "E87.2.0.3", {"start": v(77, 36) * mm, "end": v(91, 36) * mm});
            skLineSegment(sketch, "E87.2.0.4", {"start": v(91, 0) * mm, "end": v(84, 0) * mm});
            skLineSegment(sketch, "E87.3.0.0", {"start": v(133, 36) * mm, "end": v(133, 0) * mm});
            skLineSegment(sketch, "E87.3.0.1", {"start": v(119, 0) * mm, "end": v(119, 36) * mm});
            skLineSegment(sketch, "E87.3.0.2", {"start": v(126, 0) * mm, "end": v(119, 0) * mm});
            skLineSegment(sketch, "E87.3.0.3", {"start": v(119, 36) * mm, "end": v(133, 36) * mm});
            skLineSegment(sketch, "E87.3.0.4", {"start": v(133, 0) * mm, "end": v(126, 0) * mm});
            skLineSegment(sketch, "E87.4.0.0", {"start": v(175, 36) * mm, "end": v(175, 0) * mm});
            skLineSegment(sketch, "E87.4.0.1", {"start": v(161, 0) * mm, "end": v(161, 36) * mm});
            skLineSegment(sketch, "E87.4.0.2", {"start": v(168, 0) * mm, "end": v(161, 0) * mm});
            skLineSegment(sketch, "E87.4.0.3", {"start": v(161, 36) * mm, "end": v(175, 36) * mm});
            skLineSegment(sketch, "E87.4.0.4", {"start": v(175, 0) * mm, "end": v(168, 0) * mm});
            skLineSegment(sketch, "E87.5.0.0", {"start": v(217, 36) * mm, "end": v(217, 0) * mm});
            skLineSegment(sketch, "E87.5.0.1", {"start": v(203, 0) * mm, "end": v(203, 36) * mm});
            skLineSegment(sketch, "E87.5.0.2", {"start": v(210, 0) * mm, "end": v(203, 0) * mm});
            skLineSegment(sketch, "E87.5.0.3", {"start": v(203, 36) * mm, "end": v(217, 36) * mm});
            skLineSegment(sketch, "E87.5.0.4", {"start": v(217, 0) * mm, "end": v(210, 0) * mm});
            skLineSegment(sketch, "E87.6.0.0", {"start": v(259, 36) * mm, "end": v(259, 0) * mm});
            skLineSegment(sketch, "E87.6.0.1", {"start": v(245, 0) * mm, "end": v(245, 36) * mm});
            skLineSegment(sketch, "E87.6.0.2", {"start": v(252, 0) * mm, "end": v(245, 0) * mm});
            skLineSegment(sketch, "E87.6.0.3", {"start": v(245, 36) * mm, "end": v(259, 36) * mm});
            skLineSegment(sketch, "E87.6.0.4", {"start": v(259, 0) * mm, "end": v(252, 0) * mm});
            skLineSegment(sketch, "E87.7.0.0", {"start": v(301, 36) * mm, "end": v(301, 0) * mm});
            skLineSegment(sketch, "E87.7.0.1", {"start": v(287, 0) * mm, "end": v(287, 36) * mm});
            skLineSegment(sketch, "E87.7.0.2", {"start": v(294, 0) * mm, "end": v(287, 0) * mm});
            skLineSegment(sketch, "E87.7.0.3", {"start": v(287, 36) * mm, "end": v(301, 36) * mm});
            skLineSegment(sketch, "E87.7.0.4", {"start": v(301, 0) * mm, "end": v(294, 0) * mm});
            skLineSegment(sketch, "E87.8.0.0", {"start": v(343, 36) * mm, "end": v(343, 0) * mm});
            skLineSegment(sketch, "E87.8.0.1", {"start": v(329, 0) * mm, "end": v(329, 36) * mm});
            skLineSegment(sketch, "E87.8.0.2", {"start": v(336, 0) * mm, "end": v(329, 0) * mm});
            skLineSegment(sketch, "E87.8.0.3", {"start": v(329, 36) * mm, "end": v(343, 36) * mm});
            skLineSegment(sketch, "E87.8.0.4", {"start": v(343, 0) * mm, "end": v(336, 0) * mm});
            skLineSegment(sketch, "E87.direction1", {"start": v(-7, 0) * mm, "end": v(35, 0) * mm, "construction": true});
            skLineSegment(sketch, "E88.1.0.0", {"start": v(-35, 36) * mm, "end": v(-35, 0) * mm});
            skLineSegment(sketch, "E88.1.0.1", {"start": v(-49, 0) * mm, "end": v(-49, 36) * mm});
            skLineSegment(sketch, "E88.1.0.2", {"start": v(-42, 0) * mm, "end": v(-49, 0) * mm});
            skLineSegment(sketch, "E88.1.0.3", {"start": v(-49, 36) * mm, "end": v(-35, 36) * mm});
            skLineSegment(sketch, "E88.1.0.4", {"start": v(-35, 0) * mm, "end": v(-42, 0) * mm});
            skLineSegment(sketch, "E88.2.0.0", {"start": v(-77, 36) * mm, "end": v(-77, 0) * mm});
            skLineSegment(sketch, "E88.2.0.1", {"start": v(-91, 0) * mm, "end": v(-91, 36) * mm});
            skLineSegment(sketch, "E88.2.0.2", {"start": v(-84, 0) * mm, "end": v(-91, 0) * mm});
            skLineSegment(sketch, "E88.2.0.3", {"start": v(-91, 36) * mm, "end": v(-77, 36) * mm});
            skLineSegment(sketch, "E88.2.0.4", {"start": v(-77, 0) * mm, "end": v(-84, 0) * mm});
            skLineSegment(sketch, "E88.3.0.0", {"start": v(-119, 36) * mm, "end": v(-119, 0) * mm});
            skLineSegment(sketch, "E88.3.0.1", {"start": v(-133, 0) * mm, "end": v(-133, 36) * mm});
            skLineSegment(sketch, "E88.3.0.2", {"start": v(-126, 0) * mm, "end": v(-133, 0) * mm});
            skLineSegment(sketch, "E88.3.0.3", {"start": v(-133, 36) * mm, "end": v(-119, 36) * mm});
            skLineSegment(sketch, "E88.3.0.4", {"start": v(-119, 0) * mm, "end": v(-126, 0) * mm});
            skLineSegment(sketch, "E88.4.0.0", {"start": v(-161, 36) * mm, "end": v(-161, 0) * mm});
            skLineSegment(sketch, "E88.4.0.1", {"start": v(-175, 0) * mm, "end": v(-175, 36) * mm});
            skLineSegment(sketch, "E88.4.0.2", {"start": v(-168, 0) * mm, "end": v(-175, 0) * mm});
            skLineSegment(sketch, "E88.4.0.3", {"start": v(-175, 36) * mm, "end": v(-161, 36) * mm});
            skLineSegment(sketch, "E88.4.0.4", {"start": v(-161, 0) * mm, "end": v(-168, 0) * mm});
            skLineSegment(sketch, "E88.5.0.0", {"start": v(-203, 36) * mm, "end": v(-203, 0) * mm});
            skLineSegment(sketch, "E88.5.0.1", {"start": v(-217, 0) * mm, "end": v(-217, 36) * mm});
            skLineSegment(sketch, "E88.5.0.2", {"start": v(-210, 0) * mm, "end": v(-217, 0) * mm});
            skLineSegment(sketch, "E88.5.0.3", {"start": v(-217, 36) * mm, "end": v(-203, 36) * mm});
            skLineSegment(sketch, "E88.5.0.4", {"start": v(-203, 0) * mm, "end": v(-210, 0) * mm});
            skLineSegment(sketch, "E88.6.0.0", {"start": v(-245, 36) * mm, "end": v(-245, 0) * mm});
            skLineSegment(sketch, "E88.6.0.1", {"start": v(-259, 0) * mm, "end": v(-259, 36) * mm});
            skLineSegment(sketch, "E88.6.0.2", {"start": v(-252, 0) * mm, "end": v(-259, 0) * mm});
            skLineSegment(sketch, "E88.6.0.3", {"start": v(-259, 36) * mm, "end": v(-245, 36) * mm});
            skLineSegment(sketch, "E88.6.0.4", {"start": v(-245, 0) * mm, "end": v(-252, 0) * mm});
            skLineSegment(sketch, "E88.7.0.0", {"start": v(-287, 36) * mm, "end": v(-287, 0) * mm});
            skLineSegment(sketch, "E88.7.0.1", {"start": v(-301, 0) * mm, "end": v(-301, 36) * mm});
            skLineSegment(sketch, "E88.7.0.2", {"start": v(-294, 0) * mm, "end": v(-301, 0) * mm});
            skLineSegment(sketch, "E88.7.0.3", {"start": v(-301, 36) * mm, "end": v(-287, 36) * mm});
            skLineSegment(sketch, "E88.7.0.4", {"start": v(-287, 0) * mm, "end": v(-294, 0) * mm});
            skLineSegment(sketch, "E88.8.0.0", {"start": v(-329, 36) * mm, "end": v(-329, 0) * mm});
            skLineSegment(sketch, "E88.8.0.1", {"start": v(-343, 0) * mm, "end": v(-343, 36) * mm});
            skLineSegment(sketch, "E88.8.0.2", {"start": v(-336, 0) * mm, "end": v(-343, 0) * mm});
            skLineSegment(sketch, "E88.8.0.3", {"start": v(-343, 36) * mm, "end": v(-329, 36) * mm});
            skLineSegment(sketch, "E88.8.0.4", {"start": v(-329, 0) * mm, "end": v(-336, 0) * mm});
            skLineSegment(sketch, "E88.direction1", {"start": v(-7, 36) * mm, "end": v(-49, 36) * mm, "construction": true});
            skSolve(sketch);
        }
        {
            var Q0;
            Q0 = qSketchRegion(id + "F14", true);
            extrude(context, id + "F15", {"entities" : qUnion([Q0]), "operationType" : NewBodyOperationType.REMOVE, "oppositeDirection" : true, "depth" : 14 * mm});
        }
        {
            var Q0;
            Q0=qCreatedBy(makeId("Right.planeOp"),FACE);
            var sketch = newSketch(context, id + "F16", { "sketchPlane" : qUnion([Q0])});
            skLineSegment(sketch, "E89", {"start": v(0, 0) * mm, "end": v(6.7, 0) * mm});
            skPoint(sketch, "E90", {"position": v(5.5, -5.5) * mm});
            skLineSegment(sketch, "E91", {"start": v(5.5, -10) * mm, "end": v(3.61, -10) * mm});
            skPoint(sketch, "E92", {"position": v(0.55, -21.15) * mm});
            skPoint(sketch, "E93", {"position": v(30.84, -21.15) * mm});
            skLineSegment(sketch, "E94", {"start": v(0, -43) * mm, "end": v(5.5, -43) * mm});
            skPoint(sketch, "E95", {"position": v(5.5, -38.5) * mm});
            skArc(sketch, "E96", {"start": v(5.5, -10) * mm, "mid": v(9.87, -6.59) * mm, "end": v(7.61, -1.53) * mm});
            skArc(sketch, "E97", {"start": v(0.55, -21.15) * mm, "mid": v(1, -15.95) * mm, "end": v(2.34, -10.9) * mm});
            skArc(sketch, "E98", {"start": v(3.61, -10) * mm, "mid": v(2.84, -10.25) * mm, "end": v(2.34, -10.9) * mm});
            skArc(sketch, "E99", {"start": v(7.61, -1.53) * mm, "mid": v(6.94, -0.9) * mm, "end": v(6.7, 0) * mm});
            skArc(sketch, "E100", {"start": v(5.5, -43) * mm, "mid": v(9.94, -39.26) * mm, "end": v(6.99, -34.25) * mm});
            skArc(sketch, "E101", {"start": v(0.55, -21.15) * mm, "mid": v(0.74, -24.55) * mm, "end": v(1.31, -27.9) * mm});
            skArc(sketch, "E102", {"start": v(1.31, -27.9) * mm, "mid": v(3.33, -31.8) * mm, "end": v(6.99, -34.25) * mm});
            skLineSegment(sketch, "E103", {"start": v(0, -43) * mm, "end": v(0, 0) * mm});
            skSolve(sketch);
        }
        {
            var Q0;
            Q0=makeQuery(id+"F16.imprint","IMPRINT",FACE,{"disambiguationData":[TD([[makeQuery(id+"F16.imprint","IMPRINT",EDGE,{"derivedFrom":sQuery(id+"F16.wireOp",EDGE,"E89")}),-1.0]])]});
            var Q1;
            Q1=sQuery(id+"F16.wireOp",EDGE,"E89");
            revolve(context, id + "F17", {"entities" : qUnion([Q0]), "axis" : qUnion([Q1]), "revolveType" : RevolveType.FULL});
        }
        {
            var Q0;
            Q0=makeQuery(id+"F6.opPattern","COPY",FACE,{"derivedFrom":makeQuery(id+"F5.opExtrude","SWEPT_FACE",FACE,{"disambiguationData":[OSD([sQuery(id+"F4.wireOp",EDGE,"E35")])]}),"instanceName":"1"});
            var sketch = newSketch(context, id + "F18", { "sketchPlane" : qUnion([Q0])});
            skLineSegment(sketch, "E104", {"start": v(0, -108) * mm, "end": v(0, -284) * mm});
            skPoint(sketch, "E105", {"position": v(0, -196) * mm});
            skPoint(sketch, "E106", {"position": v(165, -196) * mm});
            skPoint(sketch, "E107", {"position": v(-165, -196) * mm});
            skSolve(sketch);
        }
        {
            var Q0;
            Q0=makeQuery(id+"F17.opRevolve","SWEPT_BODY",BODY,{"disambiguationData":[OSD([sQuery(id+"F16.wireOp",EDGE,"E89"),sQuery(id+"F16.wireOp",EDGE,"E91"),sQuery(id+"F16.wireOp",EDGE,"E94"),sQuery(id+"F16.wireOp",EDGE,"E96"),sQuery(id+"F16.wireOp",EDGE,"E97"),sQuery(id+"F16.wireOp",EDGE,"E98"),sQuery(id+"F16.wireOp",EDGE,"E99"),sQuery(id+"F16.wireOp",EDGE,"E100"),sQuery(id+"F16.wireOp",EDGE,"E101"),sQuery(id+"F16.wireOp",EDGE,"E102"),sQuery(id+"F16.wireOp",EDGE,"E103")])]});
            var Q1;
            Q1=qCreatedBy(makeId("Origin.pointOp"),VERTEX);
            var Q2;
            Q2=sQuery(id+"F18.wireOp",VERTEX,"E105");
            transform(context, id + "F19", {"entities" : qUnion([Q0]), "transformType" : TransformType.TRANSLATION_ENTITY, "oppositeDirectionEntity" : false, "transformLine" : qUnion([Q1, Q2]), "makeCopy" : false});
        }
        {
            var Q0;
            Q0=makeQuery(id+"F17.opRevolve","SWEPT_BODY",BODY,{"disambiguationData":[OSD([sQuery(id+"F16.wireOp",EDGE,"E89"),sQuery(id+"F16.wireOp",EDGE,"E91"),sQuery(id+"F16.wireOp",EDGE,"E94"),sQuery(id+"F16.wireOp",EDGE,"E96"),sQuery(id+"F16.wireOp",EDGE,"E97"),sQuery(id+"F16.wireOp",EDGE,"E98"),sQuery(id+"F16.wireOp",EDGE,"E99"),sQuery(id+"F16.wireOp",EDGE,"E100"),sQuery(id+"F16.wireOp",EDGE,"E101"),sQuery(id+"F16.wireOp",EDGE,"E102"),sQuery(id+"F16.wireOp",EDGE,"E103")])]});
            var Q1;
            Q1=sQuery(id+"F18.wireOp",VERTEX,"E105");
            var Q2;
            Q2=sQuery(id+"F18.wireOp",VERTEX,"E107");
            transform(context, id + "F20", {"entities" : qUnion([Q0]), "transformType" : TransformType.TRANSLATION_ENTITY, "oppositeDirectionEntity" : false, "transformLine" : qUnion([Q1, Q2]), "makeCopy" : true});
        }
        {
            var Q0;
            Q0=makeQuery(id+"F17.opRevolve","SWEPT_BODY",BODY,{"disambiguationData":[OSD([sQuery(id+"F16.wireOp",EDGE,"E89"),sQuery(id+"F16.wireOp",EDGE,"E91"),sQuery(id+"F16.wireOp",EDGE,"E94"),sQuery(id+"F16.wireOp",EDGE,"E96"),sQuery(id+"F16.wireOp",EDGE,"E97"),sQuery(id+"F16.wireOp",EDGE,"E98"),sQuery(id+"F16.wireOp",EDGE,"E99"),sQuery(id+"F16.wireOp",EDGE,"E100"),sQuery(id+"F16.wireOp",EDGE,"E101"),sQuery(id+"F16.wireOp",EDGE,"E102"),sQuery(id+"F16.wireOp",EDGE,"E103")])]});
            var Q1;
            Q1=sQuery(id+"F18.wireOp",VERTEX,"E105");
            var Q2;
            Q2=sQuery(id+"F18.wireOp",VERTEX,"E106");
            transform(context, id + "F21", {"entities" : qUnion([Q0]), "transformType" : TransformType.TRANSLATION_ENTITY, "oppositeDirectionEntity" : false, "transformLine" : qUnion([Q1, Q2]), "makeCopy" : true});
        }
        {
            var Q0;
            Q0=makeQuery(id+"F17.opRevolve","SWEPT_BODY",BODY,{"disambiguationData":[OSD([sQuery(id+"F16.wireOp",EDGE,"E89"),sQuery(id+"F16.wireOp",EDGE,"E91"),sQuery(id+"F16.wireOp",EDGE,"E94"),sQuery(id+"F16.wireOp",EDGE,"E96"),sQuery(id+"F16.wireOp",EDGE,"E97"),sQuery(id+"F16.wireOp",EDGE,"E98"),sQuery(id+"F16.wireOp",EDGE,"E99"),sQuery(id+"F16.wireOp",EDGE,"E100"),sQuery(id+"F16.wireOp",EDGE,"E101"),sQuery(id+"F16.wireOp",EDGE,"E102"),sQuery(id+"F16.wireOp",EDGE,"E103")])]});
            var Q1;
            Q1=makeQuery(id+"F20.opPattern","COPY",BODY,{"derivedFrom":makeQuery(id+"F17.opRevolve","SWEPT_BODY",BODY,{"disambiguationData":[OSD([sQuery(id+"F16.wireOp",EDGE,"E89"),sQuery(id+"F16.wireOp",EDGE,"E91"),sQuery(id+"F16.wireOp",EDGE,"E94"),sQuery(id+"F16.wireOp",EDGE,"E96"),sQuery(id+"F16.wireOp",EDGE,"E97"),sQuery(id+"F16.wireOp",EDGE,"E98"),sQuery(id+"F16.wireOp",EDGE,"E99"),sQuery(id+"F16.wireOp",EDGE,"E100"),sQuery(id+"F16.wireOp",EDGE,"E101"),sQuery(id+"F16.wireOp",EDGE,"E102"),sQuery(id+"F16.wireOp",EDGE,"E103")])]}),"instanceName":"1"});
            var Q2;
            Q2=makeQuery(id+"F21.opPattern","COPY",BODY,{"derivedFrom":makeQuery(id+"F17.opRevolve","SWEPT_BODY",BODY,{"disambiguationData":[OSD([sQuery(id+"F16.wireOp",EDGE,"E89"),sQuery(id+"F16.wireOp",EDGE,"E91"),sQuery(id+"F16.wireOp",EDGE,"E94"),sQuery(id+"F16.wireOp",EDGE,"E96"),sQuery(id+"F16.wireOp",EDGE,"E97"),sQuery(id+"F16.wireOp",EDGE,"E98"),sQuery(id+"F16.wireOp",EDGE,"E99"),sQuery(id+"F16.wireOp",EDGE,"E100"),sQuery(id+"F16.wireOp",EDGE,"E101"),sQuery(id+"F16.wireOp",EDGE,"E102"),sQuery(id+"F16.wireOp",EDGE,"E103")])]}),"instanceName":"1"});
            var Q3;
            Q3=sQuery(id+"F16.wireOp",EDGE,"E103");
            circularPattern(context, id + "F22", {"entities" : qUnion([Q0, Q1, Q2]), "axis" : qUnion([Q3]), "angle" : 360 * degree, "instanceCount" : 4, "equalSpace" : true});
        }
    });
